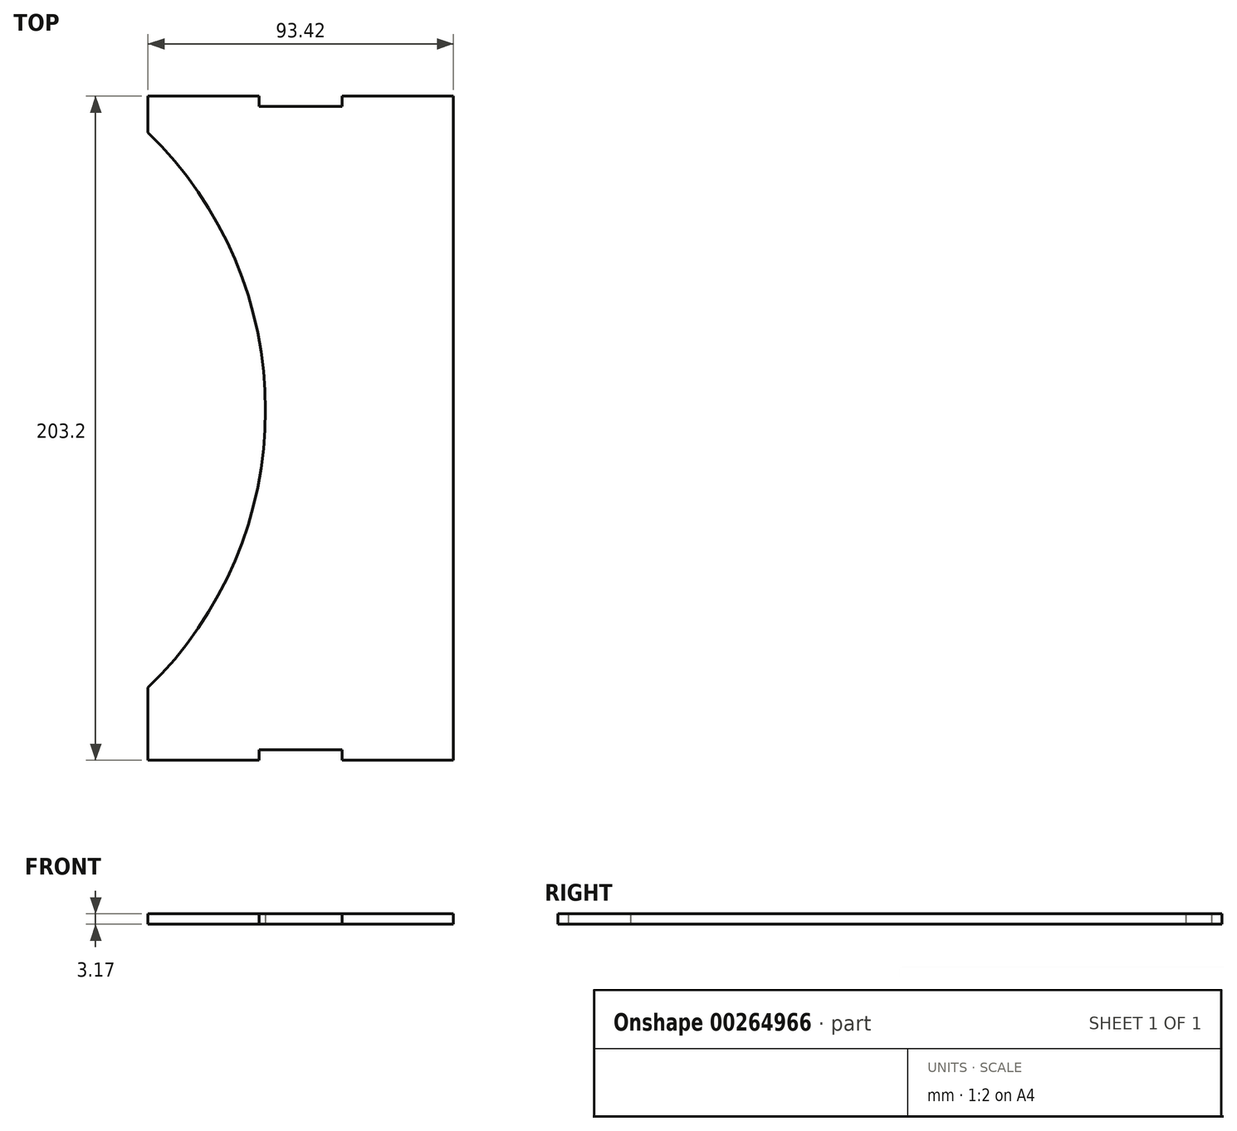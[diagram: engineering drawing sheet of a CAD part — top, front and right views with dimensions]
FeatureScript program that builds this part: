
annotation { "Feature Type Name" : "Feature", "Feature Type Description" : "" }
export const myFeature = defineFeature(function(context is Context, id is Id, definition is map)
    precondition{}
    {
        {
            var Q0;
            Q0=qCreatedBy(makeId("Top.planeOp"),FACE);
            var sketch = newSketch(context, id + "F0", { "sketchPlane" : qUnion([Q0])});
            skLineSegment(sketch, "E0", {"start": v(-42.07, -101.6) * mm, "end": v(-42.07, -79.38) * mm});
            skLineSegment(sketch, "E1", {"start": v(-42.07, -101.6) * mm, "end": v(-14.02, -101.6) * mm});
            skLineSegment(sketch, "E2.trimOffspring", {"start": v(17.34, -101.6) * mm, "end": v(51.35, -101.6) * mm});
            skLineSegment(sketch, "E3.MirrorCS", {"start": v(-42.07, 101.6) * mm, "end": v(-14.02, 101.6) * mm});
            skLineSegment(sketch, "E4.MirrorCS", {"start": v(24.58, 101.6) * mm, "end": v(51.35, 101.6) * mm});
            skPoint(sketch, "E5.endSnap0", {"position": v(38.6, 101.6) * mm});
            skLineSegment(sketch, "E6", {"start": v(50.34, -101.6) * mm, "end": v(51.35, -101.6) * mm});
            skLineSegment(sketch, "E7", {"start": v(51.35, -101.6) * mm, "end": v(51.35, 101.6) * mm});
            skPoint(sketch, "E5.end.orphan", {"position": v(49.45, 101.6) * mm});
            skLineSegment(sketch, "E8", {"start": v(-14.02, 101.6) * mm, "end": v(-13.77, 101.6) * mm});
            skLineSegment(sketch, "E9", {"start": v(-14.02, -101.6) * mm, "end": v(-13.77, -101.6) * mm});
            skLineSegment(sketch, "E10", {"start": v(-42.07, 101.6) * mm, "end": v(-42.07, 90.49) * mm});
            skPoint(sketch, "E11", {"position": v(-41.81, 5.52) * mm});
            skArc(sketch, "E12", {"start": v(-42.07, -79.38) * mm, "mid": v(-6.13, 5.56) * mm, "end": v(-42.07, 90.49) * mm});
            skLineSegment(sketch, "E13", {"start": v(-13.77, -101.6) * mm, "end": v(-8.06, -101.6) * mm});
            skLineSegment(sketch, "E14", {"start": v(-13.77, 101.6) * mm, "end": v(-8.06, 101.6) * mm});
            skPoint(sketch, "E15.orphan", {"position": v(-42.07, 104.78) * mm});
            skLineSegment(sketch, "E16", {"start": v(17.34, 101.6) * mm, "end": v(24.58, 101.6) * mm});
            skLineSegment(sketch, "E17", {"start": v(-42.07, -101.6) * mm, "end": v(-8.06, -101.6) * mm});
            skLineSegment(sketch, "E18.MirrorCS", {"start": v(-8.06, -98.43) * mm, "end": v(-8.06, -101.6) * mm});
            skLineSegment(sketch, "E19.MirrorCS", {"start": v(4.64, -98.43) * mm, "end": v(-8.06, -98.43) * mm});
            skLineSegment(sketch, "E20.MirrorCS", {"start": v(4.64, -98.43) * mm, "end": v(17.34, -98.43) * mm});
            skLineSegment(sketch, "E21.MirrorCS", {"start": v(17.34, -98.43) * mm, "end": v(17.34, -101.6) * mm});
            skLineSegment(sketch, "E22.MirrorCS", {"start": v(4.64, 98.43) * mm, "end": v(-8.06, 98.43) * mm});
            skLineSegment(sketch, "E23.MirrorCS", {"start": v(-8.06, 98.43) * mm, "end": v(-8.06, 101.6) * mm});
            skLineSegment(sketch, "E24.MirrorCS", {"start": v(4.64, 98.43) * mm, "end": v(17.34, 98.43) * mm});
            skLineSegment(sketch, "E25", {"start": v(17.34, 101.6) * mm, "end": v(17.34, 98.43) * mm});
            skLineSegment(sketch, "E26", {"start": v(-41.81, 5.52) * mm, "end": v(-41.81, 15.9) * mm});
            skSolve(sketch);
        }
        {
            var Q0;
            Q0=makeQuery(id+"F0.imprint","IMPRINT",FACE,{"disambiguationData":[TD([[makeQuery(id+"F0.imprint","IMPRINT",EDGE,{"derivedFrom":sQuery(id+"F0.wireOp",EDGE,"E0")}),-1.0]])]});
            extrude(context, id + "F1", {"entities" : qUnion([Q0]), "depth" : 3.17 * mm});
        }
    });
